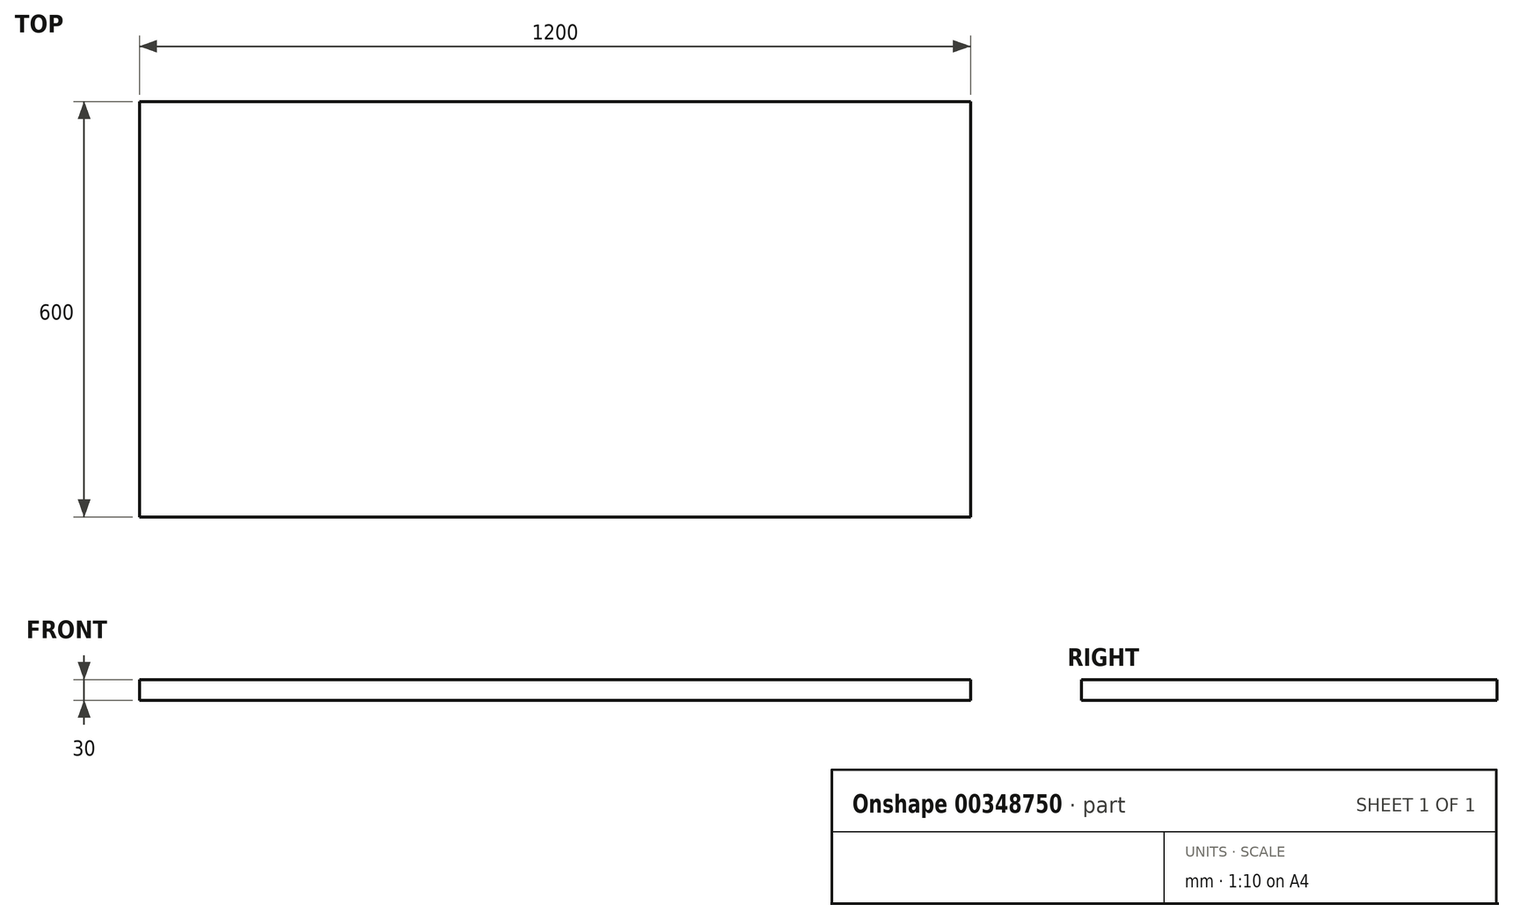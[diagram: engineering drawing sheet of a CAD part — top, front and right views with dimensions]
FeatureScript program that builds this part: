
annotation { "Feature Type Name" : "Feature", "Feature Type Description" : "" }
export const myFeature = defineFeature(function(context is Context, id is Id, definition is map)
    precondition{}
    {
        {
            var Q0;
            Q0=qCreatedBy(makeId("Top.planeOp"),FACE);
            var sketch = newSketch(context, id + "F0", { "sketchPlane" : qUnion([Q0])});
            skLineSegment(sketch, "E0.bottom", {"start": v(600, 300) * mm, "end": v(-600, 300) * mm});
            skLineSegment(sketch, "E0.top", {"start": v(600, -300) * mm, "end": v(-600, -300) * mm});
            skLineSegment(sketch, "E0.left", {"start": v(600, 300) * mm, "end": v(600, -300) * mm});
            skLineSegment(sketch, "E0.right", {"start": v(-600, 300) * mm, "end": v(-600, -300) * mm});
            skPoint(sketch, "E0.middle", {"position": v(0, 0) * mm});
            skSolve(sketch);
        }
        {
            var Q0;
            Q0 = qSketchRegion(id + "F0", true);
            extrude(context, id + "F1", {"entities" : qUnion([Q0]), "depth" : 30 * mm});
        }
    });
